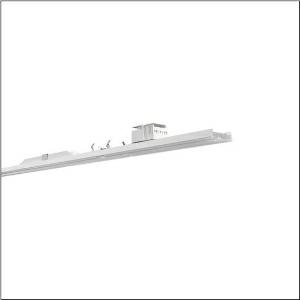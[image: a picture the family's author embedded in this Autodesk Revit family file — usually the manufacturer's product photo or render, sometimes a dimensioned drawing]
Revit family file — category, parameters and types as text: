
# Revit family: licross_r__11_recessed_ho_51tl18dn4c5l_7bc2
name_source: partatom
category: Lighting Fixtures
units: mm (PartAtom-declared; Revit-internal decimal feet)

## family parameters
Cut with Voids When Loaded = No
Host = Face
Light Source = No
Part Type = Normal
Room Calculation Point = No
Round Connector Dimension = Use Diameter
Shared = No

## types (1)
- --- (1 x LED, 12830 lm, 76 W, 4000K)
    Apparent Load = 76 VA
    CIE Flux Codes = 78 94 99 100 100
    Color Rendering = 80
    Color Temperature = 4000K
    Default Elevation = 1800 mm
    Description = Licross® 11 Recessed HOluminaire insert, length: 1.500mm, width: 66mm, height: 67mm, LED rated luminous flux: 12.830lm, light colour: 840, control gear: DALI 2, control gear: ECG DALI, with plug, 5-pole, with phase selection, mains connection: 220..240V, AC, 50/60Hz, halogen-free wiring, primary optical cover: cover, of PMMA, light emission: direct distribution, protection rating (complete): IP40, insulation class (complete): insulation class I (protective earthing), certification: CE, ENEC, VDE, protection symbol: D if used in an environment without relevant dust loads with corresponding accessories, permissible ambient temperature for indoor applications: -25..+35°C, reducing of maximum allowable ambient temperature of 5°C with ceiling mounting, corresponds to IFS (International Featured Standards) requirements for safety and quality in the food industry, packaging unit: 1 piece
    Height = 58 mm
    Lamp = 1 x LED
    Lamp Light Flux = 12830 lm
    Lamp Power = 76 W
    Lamp count = 1
    Length = 1500 mm
    Luminous efficacy = 169 lm/W
    Manufacturer = Siteco
    ModVariant = No
    Model = 51TL18DN4C5L
    Mounting Place = Ceiling
    Mounting Type = Pendant
    Number of Poles = 1
    OnlyDefault = Yes
    Power Factor = 1
    Product Name = Licross® 11 Recessed HO
    Product group = luminaire insert
    ProductGroupID = 902
    Protection Class = Protection class I
    Protection Degree = IP 40
    RLX_Detail_Level = 1
    RlxData = <blob elided: 22237 chars, md5=51967d42>
    Socket = socket
    Standby Power = 0 W
    System Light Flux = 12830 lm
    System Power = 76 W
    Type Comments = factory setting: luminous flux: 100 % | dim-lin: 254 | 430 mA
    Type Image = l_1266722.jpg
    URL = http://relux.com
    VarID = @adj_138675
    Voltage = 0 V
    Weight = 0.00 kg
    Width = 66 mm

## geometry (parser evidence)
native form markers: Blend x4, Sweep x10
no freeform markers — native parametric forms only
